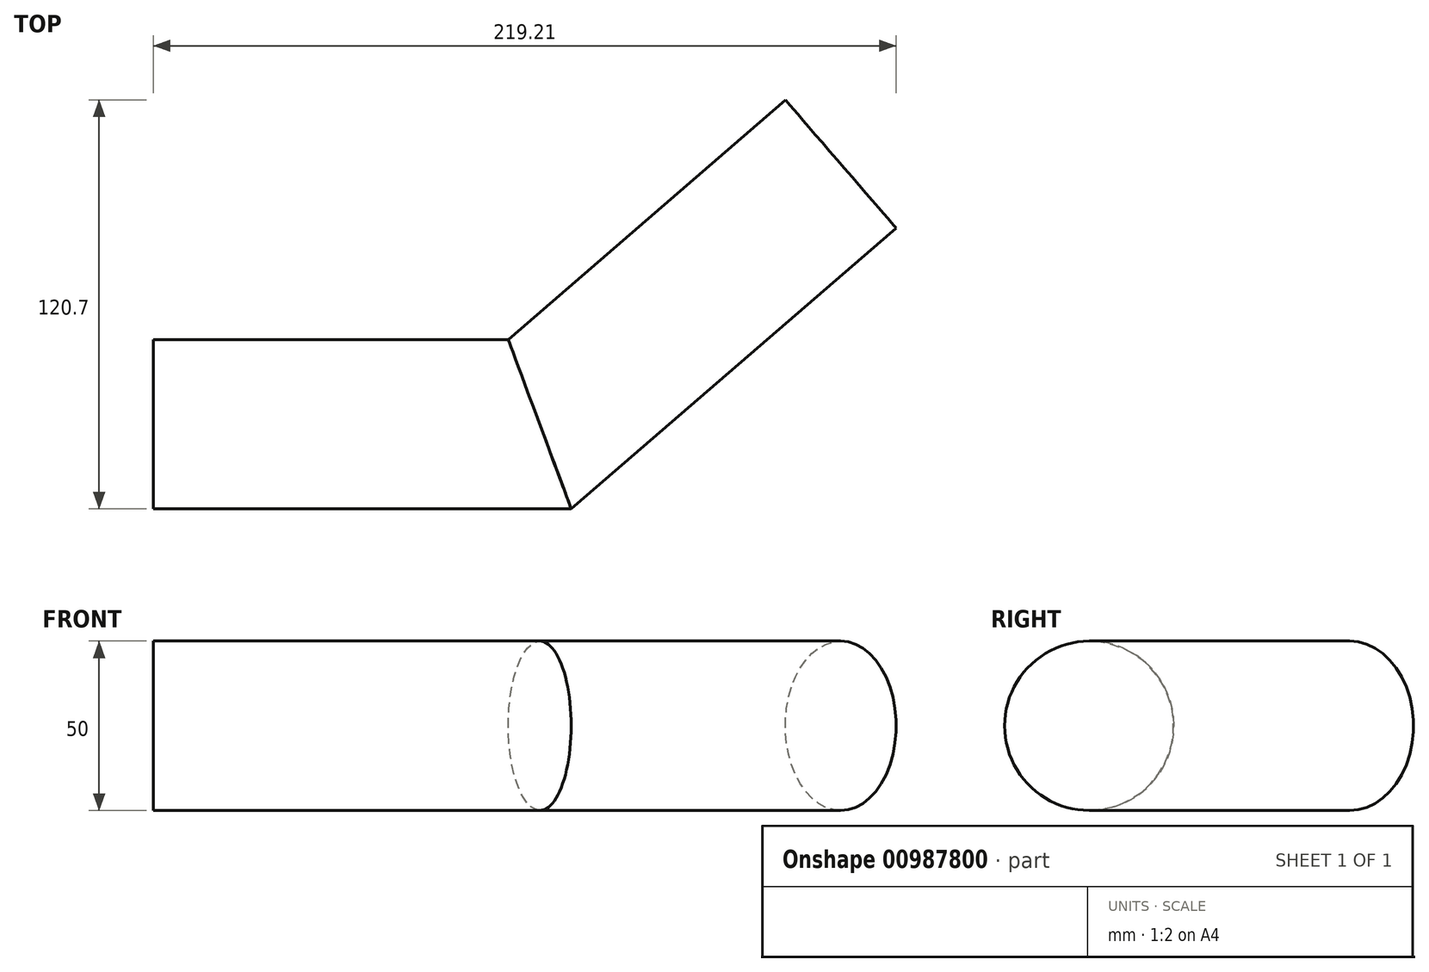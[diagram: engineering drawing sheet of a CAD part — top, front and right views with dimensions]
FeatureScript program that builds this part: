
annotation { "Feature Type Name" : "Feature", "Feature Type Description" : "" }
export const myFeature = defineFeature(function(context is Context, id is Id, definition is map)
    precondition{}
    {
        {
            var Q0;
            Q0=qCreatedBy(makeId("Top.planeOp"),FACE);
            var sketch = newSketch(context, id + "F0", { "sketchPlane" : qUnion([Q0])});
            skLineSegment(sketch, "E0", {"start": v(0, 0) * mm, "end": v(114.02, 0) * mm});
            skLineSegment(sketch, "E1", {"start": v(114.02, 0) * mm, "end": v(202.86, 76.8) * mm});
            skSolve(sketch);
        }
        {
            var Q0;
            Q0=qCreatedBy(makeId("Right.planeOp"),FACE);
            var sketch = newSketch(context, id + "F1", { "sketchPlane" : qUnion([Q0])});
            skCircle(sketch, "E2", {"center": v(0, 0) * mm, "radius": 25 * mm});
            skSolve(sketch);
        }
        {
            var Q0;
            Q0=makeQuery(id+"F1.imprint","IMPRINT",FACE,{"disambiguationData":[TD([[makeQuery(id+"F1.imprint","IMPRINT",EDGE,{"derivedFrom":sQuery(id+"F1.wireOp",EDGE,"E2")}),1.0]])]});
            var Q1;
            Q1=sQuery(id+"F0.wireOp",EDGE,"E0");
            var Q2;
            Q2=sQuery(id+"F0.wireOp",EDGE,"E1");
            sweep(context, id + "F2", {"profiles" : qUnion([Q0]), "path" : qUnion([Q1, Q2])});
        }
    });
